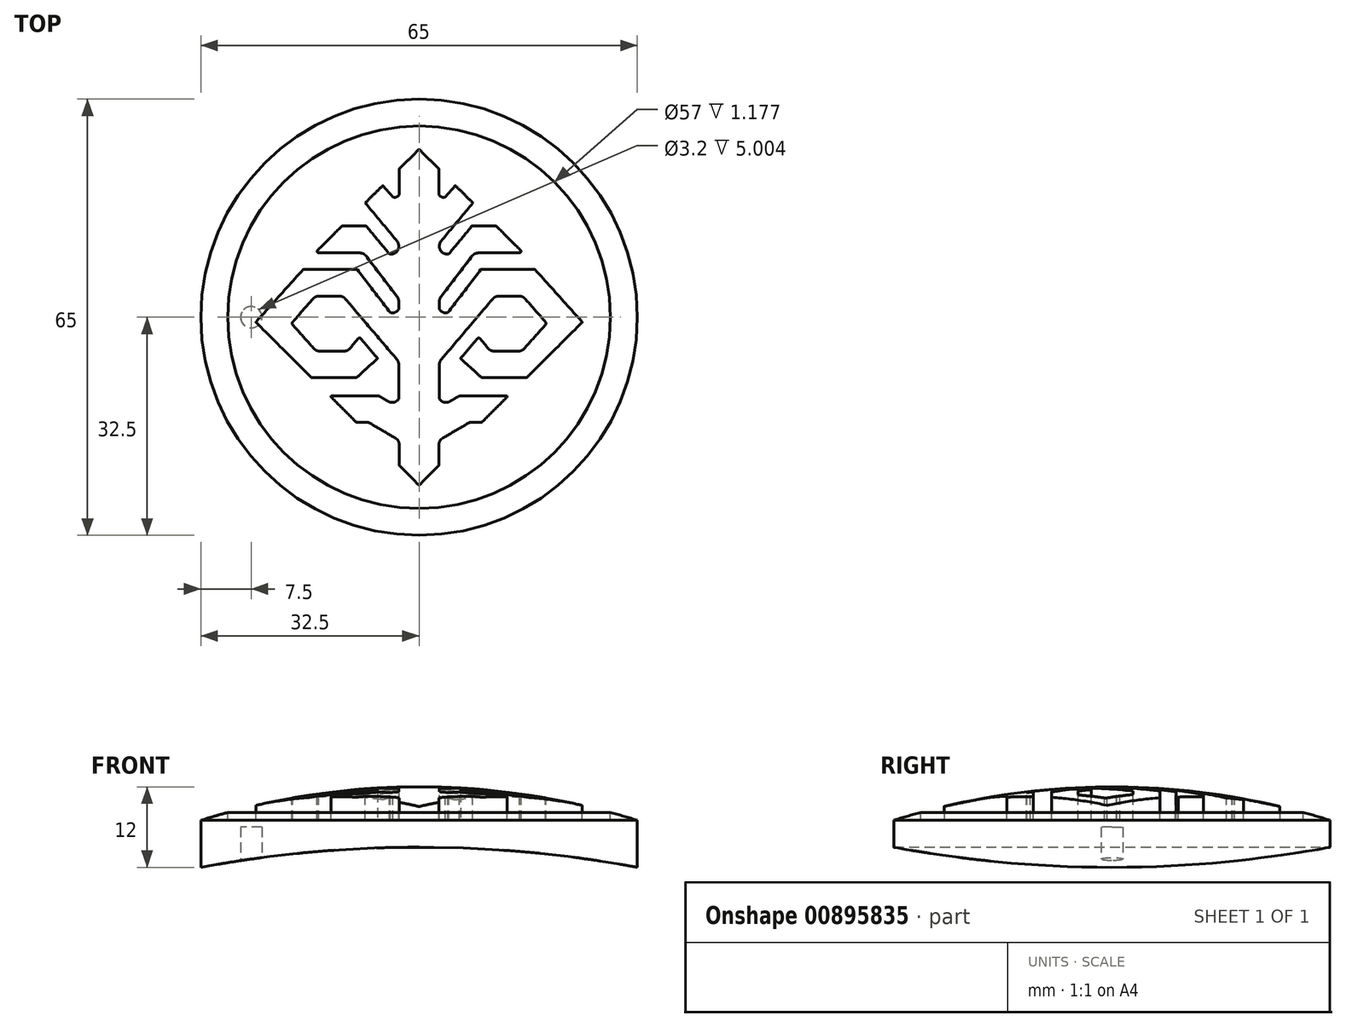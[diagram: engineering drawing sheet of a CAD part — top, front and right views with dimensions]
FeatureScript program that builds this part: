
annotation { "Feature Type Name" : "Feature", "Feature Type Description" : "" }
export const myFeature = defineFeature(function(context is Context, id is Id, definition is map)
    precondition{}
    {
        {
            var Q0;
            Q0=qCreatedBy(makeId("Top.planeOp"),FACE);
            var sketch = newSketch(context, id + "F0", { "sketchPlane" : qUnion([Q0])});
            skCircle(sketch, "E0", {"center": v(0, 0) * mm, "radius": 32.5 * mm});
            skSolve(sketch);
        }
        {
            var Q0;
            Q0=makeQuery(id+"F0.imprint","IMPRINT",FACE,{"disambiguationData":[TD([[makeQuery(id+"F0.imprint","IMPRINT",EDGE,{"derivedFrom":sQuery(id+"F0.wireOp",EDGE,"E0")}),1.0]])]});
            extrude(context, id + "F1", {"entities" : qUnion([Q0]), "oppositeDirection" : true, "depth" : 12 * mm, "offsetDistance" : 25 * mm});
        }
        {
            var Q0;
            Q0=qCreatedBy(makeId("Front.planeOp"),FACE);
            var sketch = newSketch(context, id + "F2", { "sketchPlane" : qUnion([Q0])});
            skLineSegment(sketch, "E1", {"start": v(-32.5, 8.2) * mm, "end": v(-32.5, -17.08) * mm, "construction": true});
            skLineSegment(sketch, "E2.MirrorCS", {"start": v(32.5, 8.2) * mm, "end": v(32.5, -17.08) * mm, "construction": true});
            skLineSegment(sketch, "E3", {"start": v(-38.16, -12) * mm, "end": v(47.32, -12) * mm, "construction": true});
            skArc(sketch, "E4", {"start": v(32.5, -12) * mm, "mid": v(0, -9) * mm, "end": v(-32.5, -12) * mm});
            skLineSegment(sketch, "E5", {"start": v(-32.5, -12) * mm, "end": v(-32.5, -22.63) * mm});
            skLineSegment(sketch, "E6", {"start": v(-32.5, -22.63) * mm, "end": v(32.5, -22.63) * mm});
            skLineSegment(sketch, "E7", {"start": v(32.5, -22.63) * mm, "end": v(32.5, -12) * mm});
            skSolve(sketch);
        }
        {
            var Q0;
            Q0 = qSketchRegion(id + "F2", true);
            extrude(context, id + "F3", {"entities" : qUnion([Q0]), "operationType" : NewBodyOperationType.REMOVE, "endBound" : BoundingType.SYMMETRIC, "depth" : 66 * mm, "offsetDistance" : 25 * mm});
        }
        {
            var Q0;
            Q0=qCreatedBy(makeId("Front.planeOp"),FACE);
            var sketch = newSketch(context, id + "F4", { "sketchPlane" : qUnion([Q0])});
            skLineSegment(sketch, "E8", {"start": v(-27.5, -12) * mm, "end": v(29.3, -12) * mm, "construction": true});
            skLineSegment(sketch, "E9", {"start": v(-43.42, -5) * mm, "end": v(36.93, -5) * mm, "construction": true});
            skLineSegment(sketch, "E10", {"start": v(-32.5, 9.42) * mm, "end": v(-32.5, -25.07) * mm, "construction": true});
            skLineSegment(sketch, "E11.MirrorCS", {"start": v(32.5, 9.42) * mm, "end": v(32.5, -25.07) * mm, "construction": true});
            skArc(sketch, "E12", {"start": v(32.5, -5) * mm, "mid": v(0, 0) * mm, "end": v(-32.5, -5) * mm});
            skLineSegment(sketch, "E13", {"start": v(0, 4.42) * mm, "end": v(0, -7) * mm, "construction": true});
            skLineSegment(sketch, "E14", {"start": v(0, -2.1) * mm, "end": v(0, 1.31) * mm});
            skLineSegment(sketch, "E15", {"start": v(0, 1.31) * mm, "end": v(-35.27, 1.31) * mm});
            skLineSegment(sketch, "E16", {"start": v(-35.27, 1.31) * mm, "end": v(-35.27, -5) * mm});
            skLineSegment(sketch, "E17", {"start": v(-35.27, -5) * mm, "end": v(-32.5, -5) * mm});
            skSolve(sketch);
        }
        {
            var Q0;
            {var subQ0=sQuery(id+"F4.wireOp",EDGE,"E15");Q0=makeQuery(id+"F4.imprint","IMPRINT",FACE,{"disambiguationData":[TD([[makeQuery(id+"F4.imprint","IMPRINT",EDGE,{"derivedFrom":subQ0}),1.0]])]});}
            var Q1;
            Q1=sQuery(id+"F4.wireOp",EDGE,"E13");
            revolve(context, id + "F5", {"operationType" : NewBodyOperationType.REMOVE, "surfaceOperationType" : NewSurfaceOperationType.NEW, "entities" : qUnion([Q0]), "axis" : qUnion([Q1]), "revolveType" : RevolveType.FULL, "oppositeDirection" : true});
        }
        {
            var Q0;
            Q0=makeQuery(id+"F1.opExtrude","CAP_FACE",FACE,{"disambiguationData":[OSD([sQuery(id+"F0.wireOp",EDGE,"E0")])],"isStart":true});
            var sketch = newSketch(context, id + "F6", { "sketchPlane" : qUnion([Q0])});
            skLineSegment(sketch, "E18", {"start": v(0, -25.04) * mm, "end": v(-2.96, -22.08) * mm});
            skLineSegment(sketch, "E19", {"start": v(-2.96, -22.08) * mm, "end": v(-2.96, -18.35) * mm});
            skLineSegment(sketch, "E20", {"start": v(-2.96, -18.35) * mm, "end": v(-7.6, -15.64) * mm});
            skLineSegment(sketch, "E21", {"start": v(-7.6, -15.64) * mm, "end": v(-9.37, -15.64) * mm});
            skLineSegment(sketch, "E22", {"start": v(-9.37, -15.64) * mm, "end": v(-13.27, -11.74) * mm});
            skLineSegment(sketch, "E23", {"start": v(-13.27, -11.74) * mm, "end": v(-6, -11.74) * mm});
            skLineSegment(sketch, "E24", {"start": v(-6, -11.74) * mm, "end": v(-4.42, -12.64) * mm});
            skLineSegment(sketch, "E25", {"start": v(-11.32, 3.13) * mm, "end": v(-15.46, 3.13) * mm});
            skLineSegment(sketch, "E26", {"start": v(-15.46, 3.13) * mm, "end": v(-18.84, -0.73) * mm});
            skLineSegment(sketch, "E27", {"start": v(-18.84, -1.11) * mm, "end": v(-15.32, -5.05) * mm});
            skLineSegment(sketch, "E28", {"start": v(-15.32, -5.05) * mm, "end": v(-10.62, -5.05) * mm});
            skLineSegment(sketch, "E29", {"start": v(-10.62, -5.05) * mm, "end": v(-9.05, -3.17) * mm});
            skLineSegment(sketch, "E30", {"start": v(-9.3, -8.99) * mm, "end": v(-16.06, -8.99) * mm});
            skLineSegment(sketch, "E31", {"start": v(-17.24, 7.14) * mm, "end": v(-9.23, 7.14) * mm});
            skLineSegment(sketch, "E32", {"start": v(-9.23, 7.14) * mm, "end": v(-4.3, 0.7) * mm});
            skLineSegment(sketch, "E33", {"start": v(-3.03, 2.75) * mm, "end": v(-8.25, 9.58) * mm});
            skLineSegment(sketch, "E34", {"start": v(-8.25, 9.58) * mm, "end": v(-14.94, 9.58) * mm});
            skLineSegment(sketch, "E35", {"start": v(-15.18, 9.9) * mm, "end": v(-11.46, 13.62) * mm});
            skLineSegment(sketch, "E36", {"start": v(-11.46, 13.62) * mm, "end": v(-7.9, 13.62) * mm});
            skLineSegment(sketch, "E37", {"start": v(-3.03, 10.13) * mm, "end": v(-3.03, 11.04) * mm});
            skLineSegment(sketch, "E38", {"start": v(-3.03, 11.04) * mm, "end": v(-8.01, 17.03) * mm});
            skLineSegment(sketch, "E39", {"start": v(-8.01, 17.03) * mm, "end": v(-5.4, 19.64) * mm});
            skLineSegment(sketch, "E40", {"start": v(-5.4, 19.64) * mm, "end": v(-3.94, 17.94) * mm});
            skLineSegment(sketch, "E41", {"start": v(-2.96, 18.28) * mm, "end": v(-2.96, 22.08) * mm});
            skLineSegment(sketch, "E42", {"start": v(-2.96, 22.08) * mm, "end": v(0, 25.04) * mm});
            skCircle(sketch, "E43", {"center": v(0, 0) * mm, "radius": 28.5 * mm});
            skArc(sketch, "E44", {"start": v(-4.43, 9.44) * mm, "mid": v(-3.61, 9.55) * mm, "end": v(-3.03, 10.13) * mm});
            skLineSegment(sketch, "E45", {"start": v(-7.9, 13.62) * mm, "end": v(-4.43, 9.44) * mm});
            skLineSegment(sketch, "E46", {"start": v(-3.03, 2.75) * mm, "end": v(-3.03, 1.18) * mm});
            skArc(sketch, "E47", {"start": v(-4.3, 0.7) * mm, "mid": v(-3.59, 0.72) * mm, "end": v(-3.03, 1.18) * mm});
            skLineSegment(sketch, "E48", {"start": v(-9.3, -8.99) * mm, "end": v(-6.18, -6.15) * mm});
            skArc(sketch, "E49", {"start": v(-8.7, -3.17) * mm, "mid": v(-8.88, -3.09) * mm, "end": v(-9.05, -3.17) * mm});
            skLineSegment(sketch, "E50", {"start": v(-8.7, -3.17) * mm, "end": v(-6.18, -6.15) * mm});
            skLineSegment(sketch, "E51", {"start": v(-11.32, 3.13) * mm, "end": v(-3.03, -6.61) * mm});
            skArc(sketch, "E52", {"start": v(-18.84, -0.73) * mm, "mid": v(-18.92, -0.92) * mm, "end": v(-18.84, -1.11) * mm});
            skLineSegment(sketch, "E53", {"start": v(-17.24, 7.14) * mm, "end": v(-24.3, -0.73) * mm});
            skLineSegment(sketch, "E54", {"start": v(-24.3, -0.73) * mm, "end": v(-16.06, -8.99) * mm});
            skArc(sketch, "E55", {"start": v(-15.18, 9.9) * mm, "mid": v(-15.12, 9.69) * mm, "end": v(-14.94, 9.58) * mm});
            skLineSegment(sketch, "E56", {"start": v(-3.03, -6.61) * mm, "end": v(-3.03, -12.16) * mm});
            skArc(sketch, "E57", {"start": v(-4.42, -12.64) * mm, "mid": v(-3.64, -12.66) * mm, "end": v(-3.03, -12.16) * mm});
            skArc(sketch, "E58", {"start": v(-3.94, 17.94) * mm, "mid": v(-3.37, 17.9) * mm, "end": v(-2.96, 18.28) * mm});
            skLineSegment(sketch, "E59.MirrorCS", {"start": v(17.24, 7.14) * mm, "end": v(24.3, -0.73) * mm});
            skLineSegment(sketch, "E60.MirrorCS", {"start": v(24.3, -0.73) * mm, "end": v(16.06, -8.99) * mm});
            skArc(sketch, "E61.MirrorCS", {"start": v(8.7, -3.17) * mm, "mid": v(8.88, -3.09) * mm, "end": v(9.05, -3.17) * mm});
            skArc(sketch, "E62.MirrorCS", {"start": v(18.84, -0.73) * mm, "mid": v(18.92, -0.92) * mm, "end": v(18.84, -1.11) * mm});
            skArc(sketch, "E63.MirrorCS", {"start": v(4.42, -12.64) * mm, "mid": v(3.64, -12.66) * mm, "end": v(3.03, -12.16) * mm});
            skLineSegment(sketch, "E64.MirrorCS", {"start": v(5.4, 19.64) * mm, "end": v(3.94, 17.94) * mm});
            skArc(sketch, "E65.MirrorCS", {"start": v(4.3, 0.7) * mm, "mid": v(3.59, 0.72) * mm, "end": v(3.03, 1.18) * mm});
            skArc(sketch, "E66.MirrorCS", {"start": v(4.43, 9.44) * mm, "mid": v(3.61, 9.55) * mm, "end": v(3.03, 10.13) * mm});
            skArc(sketch, "E67.MirrorCS", {"start": v(15.18, 9.9) * mm, "mid": v(15.12, 9.69) * mm, "end": v(14.94, 9.58) * mm});
            skArc(sketch, "E68.MirrorCS", {"start": v(3.94, 17.94) * mm, "mid": v(3.37, 17.9) * mm, "end": v(2.96, 18.28) * mm});
            skLineSegment(sketch, "E69.MirrorCS", {"start": v(7.6, -15.64) * mm, "end": v(9.37, -15.64) * mm});
            skLineSegment(sketch, "E70.MirrorCS", {"start": v(3.03, 10.13) * mm, "end": v(3.03, 11.04) * mm});
            skLineSegment(sketch, "E71.MirrorCS", {"start": v(3.03, 2.75) * mm, "end": v(3.03, 1.18) * mm});
            skLineSegment(sketch, "E72.MirrorCS", {"start": v(10.62, -5.05) * mm, "end": v(9.05, -3.17) * mm});
            skLineSegment(sketch, "E73.MirrorCS", {"start": v(6, -11.74) * mm, "end": v(4.42, -12.64) * mm});
            skLineSegment(sketch, "E74.MirrorCS", {"start": v(17.24, 7.14) * mm, "end": v(9.23, 7.14) * mm});
            skLineSegment(sketch, "E75.MirrorCS", {"start": v(9.3, -8.99) * mm, "end": v(16.06, -8.99) * mm});
            skLineSegment(sketch, "E76.MirrorCS", {"start": v(3.03, -6.61) * mm, "end": v(3.03, -12.16) * mm});
            skLineSegment(sketch, "E77.MirrorCS", {"start": v(8.01, 17.03) * mm, "end": v(5.4, 19.64) * mm});
            skLineSegment(sketch, "E78.MirrorCS", {"start": v(8.25, 9.58) * mm, "end": v(14.94, 9.58) * mm});
            skLineSegment(sketch, "E79.MirrorCS", {"start": v(11.46, 13.62) * mm, "end": v(7.9, 13.62) * mm});
            skLineSegment(sketch, "E80.MirrorCS", {"start": v(2.96, 18.28) * mm, "end": v(2.96, 22.08) * mm});
            skLineSegment(sketch, "E81.MirrorCS", {"start": v(3.03, 11.04) * mm, "end": v(8.01, 17.03) * mm});
            skLineSegment(sketch, "E82.MirrorCS", {"start": v(15.46, 3.13) * mm, "end": v(18.84, -0.73) * mm});
            skLineSegment(sketch, "E83.MirrorCS", {"start": v(9.3, -8.99) * mm, "end": v(6.18, -6.15) * mm});
            skLineSegment(sketch, "E84.MirrorCS", {"start": v(9.37, -15.64) * mm, "end": v(13.27, -11.74) * mm});
            skLineSegment(sketch, "E85.MirrorCS", {"start": v(15.32, -5.05) * mm, "end": v(10.62, -5.05) * mm});
            skLineSegment(sketch, "E86.MirrorCS", {"start": v(2.96, 22.08) * mm, "end": v(0, 25.04) * mm});
            skLineSegment(sketch, "E87.MirrorCS", {"start": v(3.03, 2.75) * mm, "end": v(8.25, 9.58) * mm});
            skLineSegment(sketch, "E88.MirrorCS", {"start": v(2.96, -18.35) * mm, "end": v(7.6, -15.64) * mm});
            skLineSegment(sketch, "E89.MirrorCS", {"start": v(13.27, -11.74) * mm, "end": v(6, -11.74) * mm});
            skLineSegment(sketch, "E90.MirrorCS", {"start": v(9.23, 7.14) * mm, "end": v(4.3, 0.7) * mm});
            skLineSegment(sketch, "E91.MirrorCS", {"start": v(7.9, 13.62) * mm, "end": v(4.43, 9.44) * mm});
            skLineSegment(sketch, "E92.MirrorCS", {"start": v(8.7, -3.17) * mm, "end": v(6.18, -6.15) * mm});
            skLineSegment(sketch, "E93.MirrorCS", {"start": v(15.18, 9.9) * mm, "end": v(11.46, 13.62) * mm});
            skLineSegment(sketch, "E94.MirrorCS", {"start": v(18.84, -1.11) * mm, "end": v(15.32, -5.05) * mm});
            skLineSegment(sketch, "E95.MirrorCS", {"start": v(11.32, 3.13) * mm, "end": v(3.03, -6.61) * mm});
            skLineSegment(sketch, "E96.MirrorCS", {"start": v(2.96, -22.08) * mm, "end": v(2.96, -18.35) * mm});
            skLineSegment(sketch, "E97.MirrorCS", {"start": v(0, -25.04) * mm, "end": v(2.96, -22.08) * mm});
            skLineSegment(sketch, "E98.MirrorCS", {"start": v(11.32, 3.13) * mm, "end": v(15.46, 3.13) * mm});
            skSolve(sketch);
        }
        {
            var Q0;
            Q0 = qSketchRegion(id + "F6", true);
            extrude(context, id + "F7", {"entities" : qUnion([Q0]), "operationType" : NewBodyOperationType.REMOVE, "oppositeDirection" : true, "depth" : 5 * mm, "offsetDistance" : 25 * mm});
        }
        {
            var Q0;
            Q0=makeQuery(id+"F7.boolean.opBoolean","COPY",EDGE,{"derivedFrom":makeQuery(id+"F7.opExtrude","SWEPT_EDGE",EDGE,{"disambiguationData":[OSD([sQuery(id+"F6.wireOp",EDGE,"E70.MirrorCS"),sQuery(id+"F6.wireOp",EDGE,"E81.MirrorCS")])]})});
            var Q1;
            Q1=makeQuery(id+"F7.boolean.opBoolean","COPY",EDGE,{"derivedFrom":makeQuery(id+"F7.opExtrude","SWEPT_EDGE",EDGE,{"disambiguationData":[OSD([sQuery(id+"F6.wireOp",EDGE,"E66.MirrorCS"),sQuery(id+"F6.wireOp",EDGE,"E70.MirrorCS")])]})});
            var Q2;
            Q2=makeQuery(id+"F7.boolean.opBoolean","COPY",EDGE,{"derivedFrom":makeQuery(id+"F7.opExtrude","SWEPT_EDGE",EDGE,{"disambiguationData":[OSD([sQuery(id+"F6.wireOp",EDGE,"E37"),sQuery(id+"F6.wireOp",EDGE,"E38")])]})});
            var Q3;
            Q3=makeQuery(id+"F7.boolean.opBoolean","COPY",EDGE,{"derivedFrom":makeQuery(id+"F7.opExtrude","SWEPT_EDGE",EDGE,{"disambiguationData":[OSD([sQuery(id+"F6.wireOp",EDGE,"E37"),sQuery(id+"F6.wireOp",EDGE,"E44")])]})});
            var Q4;
            Q4=makeQuery(id+"F7.boolean.opBoolean","COPY",EDGE,{"derivedFrom":makeQuery(id+"F7.opExtrude","SWEPT_EDGE",EDGE,{"disambiguationData":[OSD([sQuery(id+"F6.wireOp",EDGE,"E71.MirrorCS"),sQuery(id+"F6.wireOp",EDGE,"E87.MirrorCS")])]})});
            var Q5;
            Q5=makeQuery(id+"F7.boolean.opBoolean","COPY",EDGE,{"derivedFrom":makeQuery(id+"F7.opExtrude","SWEPT_EDGE",EDGE,{"disambiguationData":[OSD([sQuery(id+"F6.wireOp",EDGE,"E33"),sQuery(id+"F6.wireOp",EDGE,"E46")])]})});
            var Q6;
            Q6=makeQuery(id+"F7.boolean.opBoolean","COPY",EDGE,{"derivedFrom":makeQuery(id+"F7.opExtrude","SWEPT_EDGE",EDGE,{"disambiguationData":[OSD([sQuery(id+"F6.wireOp",EDGE,"E33"),sQuery(id+"F6.wireOp",EDGE,"E34")])]})});
            var Q7;
            Q7=makeQuery(id+"F7.boolean.opBoolean","COPY",EDGE,{"derivedFrom":makeQuery(id+"F7.opExtrude","SWEPT_EDGE",EDGE,{"disambiguationData":[OSD([sQuery(id+"F6.wireOp",EDGE,"E78.MirrorCS"),sQuery(id+"F6.wireOp",EDGE,"E87.MirrorCS")])]})});
            var Q8;
            Q8=makeQuery(id+"F7.boolean.opBoolean","COPY",EDGE,{"derivedFrom":makeQuery(id+"F7.opExtrude","SWEPT_EDGE",EDGE,{"disambiguationData":[OSD([sQuery(id+"F6.wireOp",EDGE,"E95.MirrorCS"),sQuery(id+"F6.wireOp",EDGE,"E98.MirrorCS")])]})});
            var Q9;
            Q9=makeQuery(id+"F7.boolean.opBoolean","COPY",EDGE,{"derivedFrom":makeQuery(id+"F7.opExtrude","SWEPT_EDGE",EDGE,{"disambiguationData":[OSD([sQuery(id+"F6.wireOp",EDGE,"E82.MirrorCS"),sQuery(id+"F6.wireOp",EDGE,"E98.MirrorCS")])]})});
            var Q10;
            Q10=makeQuery(id+"F7.boolean.opBoolean","COPY",EDGE,{"derivedFrom":makeQuery(id+"F7.opExtrude","SWEPT_EDGE",EDGE,{"disambiguationData":[OSD([sQuery(id+"F6.wireOp",EDGE,"E25"),sQuery(id+"F6.wireOp",EDGE,"E51")])]})});
            var Q11;
            Q11=makeQuery(id+"F7.boolean.opBoolean","COPY",EDGE,{"derivedFrom":makeQuery(id+"F7.opExtrude","SWEPT_EDGE",EDGE,{"disambiguationData":[OSD([sQuery(id+"F6.wireOp",EDGE,"E25"),sQuery(id+"F6.wireOp",EDGE,"E26")])]})});
            var Q12;
            Q12=makeQuery(id+"F7.boolean.opBoolean","COPY",EDGE,{"derivedFrom":makeQuery(id+"F7.opExtrude","SWEPT_EDGE",EDGE,{"disambiguationData":[OSD([sQuery(id+"F6.wireOp",EDGE,"E72.MirrorCS"),sQuery(id+"F6.wireOp",EDGE,"E85.MirrorCS")])]})});
            var Q13;
            Q13=makeQuery(id+"F7.boolean.opBoolean","COPY",EDGE,{"derivedFrom":makeQuery(id+"F7.opExtrude","SWEPT_EDGE",EDGE,{"disambiguationData":[OSD([sQuery(id+"F6.wireOp",EDGE,"E85.MirrorCS"),sQuery(id+"F6.wireOp",EDGE,"E94.MirrorCS")])]})});
            var Q14;
            Q14=makeQuery(id+"F7.boolean.opBoolean","COPY",EDGE,{"derivedFrom":makeQuery(id+"F7.opExtrude","SWEPT_EDGE",EDGE,{"disambiguationData":[OSD([sQuery(id+"F6.wireOp",EDGE,"E28"),sQuery(id+"F6.wireOp",EDGE,"E29")])]})});
            var Q15;
            Q15=makeQuery(id+"F7.boolean.opBoolean","COPY",EDGE,{"derivedFrom":makeQuery(id+"F7.opExtrude","SWEPT_EDGE",EDGE,{"disambiguationData":[OSD([sQuery(id+"F6.wireOp",EDGE,"E27"),sQuery(id+"F6.wireOp",EDGE,"E28")])]})});
            var Q16;
            Q16=makeQuery(id+"F7.boolean.opBoolean","COPY",EDGE,{"derivedFrom":makeQuery(id+"F7.opExtrude","SWEPT_EDGE",EDGE,{"disambiguationData":[OSD([sQuery(id+"F6.wireOp",EDGE,"E51"),sQuery(id+"F6.wireOp",EDGE,"E56")])]})});
            var Q17;
            Q17=makeQuery(id+"F7.boolean.opBoolean","COPY",EDGE,{"derivedFrom":makeQuery(id+"F7.opExtrude","SWEPT_EDGE",EDGE,{"disambiguationData":[OSD([sQuery(id+"F6.wireOp",EDGE,"E76.MirrorCS"),sQuery(id+"F6.wireOp",EDGE,"E95.MirrorCS")])]})});
            var Q18;
            Q18=makeQuery(id+"F7.boolean.opBoolean","COPY",EDGE,{"derivedFrom":makeQuery(id+"F7.opExtrude","SWEPT_EDGE",EDGE,{"disambiguationData":[OSD([sQuery(id+"F6.wireOp",EDGE,"E69.MirrorCS"),sQuery(id+"F6.wireOp",EDGE,"E88.MirrorCS")])]})});
            var Q19;
            Q19=makeQuery(id+"F7.boolean.opBoolean","COPY",EDGE,{"derivedFrom":makeQuery(id+"F7.opExtrude","SWEPT_EDGE",EDGE,{"disambiguationData":[OSD([sQuery(id+"F6.wireOp",EDGE,"E88.MirrorCS"),sQuery(id+"F6.wireOp",EDGE,"E96.MirrorCS")])]})});
            var Q20;
            Q20=makeQuery(id+"F7.boolean.opBoolean","COPY",EDGE,{"derivedFrom":makeQuery(id+"F7.opExtrude","SWEPT_EDGE",EDGE,{"disambiguationData":[OSD([sQuery(id+"F6.wireOp",EDGE,"E19"),sQuery(id+"F6.wireOp",EDGE,"E20")])]})});
            var Q21;
            Q21=makeQuery(id+"F7.boolean.opBoolean","COPY",EDGE,{"derivedFrom":makeQuery(id+"F7.opExtrude","SWEPT_EDGE",EDGE,{"disambiguationData":[OSD([sQuery(id+"F6.wireOp",EDGE,"E20"),sQuery(id+"F6.wireOp",EDGE,"E21")])]})});
            fillet(context, id + "F8", {"entities" : qUnion([Q0, Q1, Q2, Q3, Q4, Q5, Q6, Q7, Q8, Q9, Q10, Q11, Q12, Q13, Q14, Q15, Q16, Q17, Q18, Q19, Q20, Q21]), "radius" : 1.1 * mm, "tangentPropagation" : true, "allowEdgeOverflow" : false});
        }
        {
            var Q0;
            Q0=makeQuery(id+"F7.boolean.opBoolean","COPY",EDGE,{"derivedFrom":makeQuery(id+"F7.opExtrude","SWEPT_EDGE",EDGE,{"disambiguationData":[OSD([sQuery(id+"F6.wireOp",EDGE,"E18"),sQuery(id+"F6.wireOp",EDGE,"E97.MirrorCS")])]})});
            var Q1;
            Q1=makeQuery(id+"F7.boolean.opBoolean","COPY",EDGE,{"derivedFrom":makeQuery(id+"F7.opExtrude","SWEPT_EDGE",EDGE,{"disambiguationData":[OSD([sQuery(id+"F6.wireOp",EDGE,"E18"),sQuery(id+"F6.wireOp",EDGE,"E19")])]})});
            var Q2;
            Q2=makeQuery(id+"F7.boolean.opBoolean","COPY",EDGE,{"derivedFrom":makeQuery(id+"F7.opExtrude","SWEPT_EDGE",EDGE,{"disambiguationData":[OSD([sQuery(id+"F6.wireOp",EDGE,"E21"),sQuery(id+"F6.wireOp",EDGE,"E22")])]})});
            var Q3;
            Q3=makeQuery(id+"F7.boolean.opBoolean","COPY",EDGE,{"derivedFrom":makeQuery(id+"F7.opExtrude","SWEPT_EDGE",EDGE,{"disambiguationData":[OSD([sQuery(id+"F6.wireOp",EDGE,"E22"),sQuery(id+"F6.wireOp",EDGE,"E23")])]})});
            var Q4;
            Q4=makeQuery(id+"F7.boolean.opBoolean","COPY",EDGE,{"derivedFrom":makeQuery(id+"F7.opExtrude","SWEPT_EDGE",EDGE,{"disambiguationData":[OSD([sQuery(id+"F6.wireOp",EDGE,"E23"),sQuery(id+"F6.wireOp",EDGE,"E24")])]})});
            var Q5;
            Q5=makeQuery(id+"F7.boolean.opBoolean","COPY",EDGE,{"derivedFrom":makeQuery(id+"F7.opExtrude","SWEPT_EDGE",EDGE,{"disambiguationData":[OSD([sQuery(id+"F6.wireOp",EDGE,"E48"),sQuery(id+"F6.wireOp",EDGE,"E50")])]})});
            var Q6;
            Q6=makeQuery(id+"F7.boolean.opBoolean","COPY",EDGE,{"derivedFrom":makeQuery(id+"F7.opExtrude","SWEPT_EDGE",EDGE,{"disambiguationData":[OSD([sQuery(id+"F6.wireOp",EDGE,"E30"),sQuery(id+"F6.wireOp",EDGE,"E48")])]})});
            var Q7;
            Q7=makeQuery(id+"F7.boolean.opBoolean","COPY",EDGE,{"derivedFrom":makeQuery(id+"F7.opExtrude","SWEPT_EDGE",EDGE,{"disambiguationData":[OSD([sQuery(id+"F6.wireOp",EDGE,"E30"),sQuery(id+"F6.wireOp",EDGE,"E54")])]})});
            var Q8;
            Q8=makeQuery(id+"F7.boolean.opBoolean","COPY",EDGE,{"derivedFrom":makeQuery(id+"F7.opExtrude","SWEPT_EDGE",EDGE,{"disambiguationData":[OSD([sQuery(id+"F6.wireOp",EDGE,"E53"),sQuery(id+"F6.wireOp",EDGE,"E54")])]})});
            var Q9;
            Q9=makeQuery(id+"F7.boolean.opBoolean","COPY",EDGE,{"derivedFrom":makeQuery(id+"F7.opExtrude","SWEPT_EDGE",EDGE,{"disambiguationData":[OSD([sQuery(id+"F6.wireOp",EDGE,"E31"),sQuery(id+"F6.wireOp",EDGE,"E53")])]})});
            var Q10;
            Q10=makeQuery(id+"F7.boolean.opBoolean","COPY",EDGE,{"derivedFrom":makeQuery(id+"F7.opExtrude","SWEPT_EDGE",EDGE,{"disambiguationData":[OSD([sQuery(id+"F6.wireOp",EDGE,"E31"),sQuery(id+"F6.wireOp",EDGE,"E32")])]})});
            var Q11;
            Q11=makeQuery(id+"F7.boolean.opBoolean","COPY",EDGE,{"derivedFrom":makeQuery(id+"F7.opExtrude","SWEPT_EDGE",EDGE,{"disambiguationData":[OSD([sQuery(id+"F6.wireOp",EDGE,"E35"),sQuery(id+"F6.wireOp",EDGE,"E36")])]})});
            var Q12;
            Q12=makeQuery(id+"F7.boolean.opBoolean","COPY",EDGE,{"derivedFrom":makeQuery(id+"F7.opExtrude","SWEPT_EDGE",EDGE,{"disambiguationData":[OSD([sQuery(id+"F6.wireOp",EDGE,"E36"),sQuery(id+"F6.wireOp",EDGE,"E45")])]})});
            var Q13;
            Q13=makeQuery(id+"F7.boolean.opBoolean","COPY",EDGE,{"derivedFrom":makeQuery(id+"F7.opExtrude","SWEPT_EDGE",EDGE,{"disambiguationData":[OSD([sQuery(id+"F6.wireOp",EDGE,"E39"),sQuery(id+"F6.wireOp",EDGE,"E40")])]})});
            var Q14;
            Q14=makeQuery(id+"F7.boolean.opBoolean","COPY",EDGE,{"derivedFrom":makeQuery(id+"F7.opExtrude","SWEPT_EDGE",EDGE,{"disambiguationData":[OSD([sQuery(id+"F6.wireOp",EDGE,"E41"),sQuery(id+"F6.wireOp",EDGE,"E42")])]})});
            var Q15;
            Q15=makeQuery(id+"F7.boolean.opBoolean","COPY",EDGE,{"derivedFrom":makeQuery(id+"F7.opExtrude","SWEPT_EDGE",EDGE,{"disambiguationData":[OSD([sQuery(id+"F6.wireOp",EDGE,"E42"),sQuery(id+"F6.wireOp",EDGE,"E86.MirrorCS")])]})});
            var Q16;
            Q16=makeQuery(id+"F7.boolean.opBoolean","COPY",EDGE,{"derivedFrom":makeQuery(id+"F7.opExtrude","SWEPT_EDGE",EDGE,{"disambiguationData":[OSD([sQuery(id+"F6.wireOp",EDGE,"E80.MirrorCS"),sQuery(id+"F6.wireOp",EDGE,"E86.MirrorCS")])]})});
            var Q17;
            Q17=makeQuery(id+"F7.boolean.opBoolean","COPY",EDGE,{"derivedFrom":makeQuery(id+"F7.opExtrude","SWEPT_EDGE",EDGE,{"disambiguationData":[OSD([sQuery(id+"F6.wireOp",EDGE,"E64.MirrorCS"),sQuery(id+"F6.wireOp",EDGE,"E77.MirrorCS")])]})});
            var Q18;
            Q18=makeQuery(id+"F7.boolean.opBoolean","COPY",EDGE,{"derivedFrom":makeQuery(id+"F7.opExtrude","SWEPT_EDGE",EDGE,{"disambiguationData":[OSD([sQuery(id+"F6.wireOp",EDGE,"E77.MirrorCS"),sQuery(id+"F6.wireOp",EDGE,"E81.MirrorCS")])]})});
            var Q19;
            Q19=makeQuery(id+"F7.boolean.opBoolean","COPY",EDGE,{"derivedFrom":makeQuery(id+"F7.opExtrude","SWEPT_EDGE",EDGE,{"disambiguationData":[OSD([sQuery(id+"F6.wireOp",EDGE,"E79.MirrorCS"),sQuery(id+"F6.wireOp",EDGE,"E91.MirrorCS")])]})});
            var Q20;
            Q20=makeQuery(id+"F7.boolean.opBoolean","COPY",EDGE,{"derivedFrom":makeQuery(id+"F7.opExtrude","SWEPT_EDGE",EDGE,{"disambiguationData":[OSD([sQuery(id+"F6.wireOp",EDGE,"E79.MirrorCS"),sQuery(id+"F6.wireOp",EDGE,"E93.MirrorCS")])]})});
            var Q21;
            Q21=makeQuery(id+"F7.boolean.opBoolean","COPY",EDGE,{"derivedFrom":makeQuery(id+"F7.opExtrude","SWEPT_EDGE",EDGE,{"disambiguationData":[OSD([sQuery(id+"F6.wireOp",EDGE,"E74.MirrorCS"),sQuery(id+"F6.wireOp",EDGE,"E90.MirrorCS")])]})});
            var Q22;
            Q22=makeQuery(id+"F7.boolean.opBoolean","COPY",EDGE,{"derivedFrom":makeQuery(id+"F7.opExtrude","SWEPT_EDGE",EDGE,{"disambiguationData":[OSD([sQuery(id+"F6.wireOp",EDGE,"E59.MirrorCS"),sQuery(id+"F6.wireOp",EDGE,"E74.MirrorCS")])]})});
            var Q23;
            Q23=makeQuery(id+"F7.boolean.opBoolean","COPY",EDGE,{"derivedFrom":makeQuery(id+"F7.opExtrude","SWEPT_EDGE",EDGE,{"disambiguationData":[OSD([sQuery(id+"F6.wireOp",EDGE,"E59.MirrorCS"),sQuery(id+"F6.wireOp",EDGE,"E60.MirrorCS")])]})});
            var Q24;
            Q24=makeQuery(id+"F7.boolean.opBoolean","COPY",EDGE,{"derivedFrom":makeQuery(id+"F7.opExtrude","SWEPT_EDGE",EDGE,{"disambiguationData":[OSD([sQuery(id+"F6.wireOp",EDGE,"E83.MirrorCS"),sQuery(id+"F6.wireOp",EDGE,"E92.MirrorCS")])]})});
            var Q25;
            Q25=makeQuery(id+"F7.boolean.opBoolean","COPY",EDGE,{"derivedFrom":makeQuery(id+"F7.opExtrude","SWEPT_EDGE",EDGE,{"disambiguationData":[OSD([sQuery(id+"F6.wireOp",EDGE,"E75.MirrorCS"),sQuery(id+"F6.wireOp",EDGE,"E83.MirrorCS")])]})});
            var Q26;
            Q26=makeQuery(id+"F7.boolean.opBoolean","COPY",EDGE,{"derivedFrom":makeQuery(id+"F7.opExtrude","SWEPT_EDGE",EDGE,{"disambiguationData":[OSD([sQuery(id+"F6.wireOp",EDGE,"E60.MirrorCS"),sQuery(id+"F6.wireOp",EDGE,"E75.MirrorCS")])]})});
            var Q27;
            Q27=makeQuery(id+"F7.boolean.opBoolean","COPY",EDGE,{"derivedFrom":makeQuery(id+"F7.opExtrude","SWEPT_EDGE",EDGE,{"disambiguationData":[OSD([sQuery(id+"F6.wireOp",EDGE,"E84.MirrorCS"),sQuery(id+"F6.wireOp",EDGE,"E89.MirrorCS")])]})});
            var Q28;
            Q28=makeQuery(id+"F7.boolean.opBoolean","COPY",EDGE,{"derivedFrom":makeQuery(id+"F7.opExtrude","SWEPT_EDGE",EDGE,{"disambiguationData":[OSD([sQuery(id+"F6.wireOp",EDGE,"E69.MirrorCS"),sQuery(id+"F6.wireOp",EDGE,"E84.MirrorCS")])]})});
            var Q29;
            Q29=makeQuery(id+"F7.boolean.opBoolean","COPY",EDGE,{"derivedFrom":makeQuery(id+"F7.opExtrude","SWEPT_EDGE",EDGE,{"disambiguationData":[OSD([sQuery(id+"F6.wireOp",EDGE,"E96.MirrorCS"),sQuery(id+"F6.wireOp",EDGE,"E97.MirrorCS")])]})});
            fillet(context, id + "F9", {"entities" : qUnion([Q0, Q1, Q2, Q3, Q4, Q5, Q6, Q7, Q8, Q9, Q10, Q11, Q12, Q13, Q14, Q15, Q16, Q17, Q18, Q19, Q20, Q21, Q22, Q23, Q24, Q25, Q26, Q27, Q28, Q29]), "radius" : 0.1 * mm, "tangentPropagation" : true, "allowEdgeOverflow" : false});
        }
        {
            var Q0;
            Q0=qCreatedBy(makeId("Top.planeOp"),FACE);
            cPlane(context, id + "F10", {"entities" : qUnion([Q0]), "cplaneType" : CPlaneType.OFFSET, "offset" : 12 * mm, "oppositeDirection" : true, "width" : 150 * mm, "height" : 150 * mm});
        }
        {
            var Q0;
            Q0=qCreatedBy(id+"F10.planeOp",FACE);
            var sketch = newSketch(context, id + "F11", { "sketchPlane" : qUnion([Q0])});
            skCircle(sketch, "E99", {"center": v(-25, 0) * mm, "radius": 1.6 * mm});
            skCircle(sketch, "E100.MirrorC", {"center": v(25, 0) * mm, "radius": 1.6 * mm});
            skSolve(sketch);
        }
        {
            var Q0;
            Q0=makeQuery(id+"F11.imprint","IMPRINT",FACE,{"disambiguationData":[TD([[makeQuery(id+"F11.imprint","IMPRINT",EDGE,{"derivedFrom":sQuery(id+"F11.wireOp",EDGE,"E99")}),1.0]])]});
            var Q1;
            Q1=makeQuery(id+"F11.imprint","IMPRINT",FACE,{"disambiguationData":[TD([[makeQuery(id+"F11.imprint","IMPRINT",EDGE,{"derivedFrom":sQuery(id+"F11.wireOp",EDGE,"E100.MirrorC")}),-1.0]])]});
            extrude(context, id + "F12", {"entities" : qUnion([Q0, Q1]), "operationType" : NewBodyOperationType.REMOVE, "depth" : (6) * mm, "offsetDistance" : 25 * mm});
        }
    });
